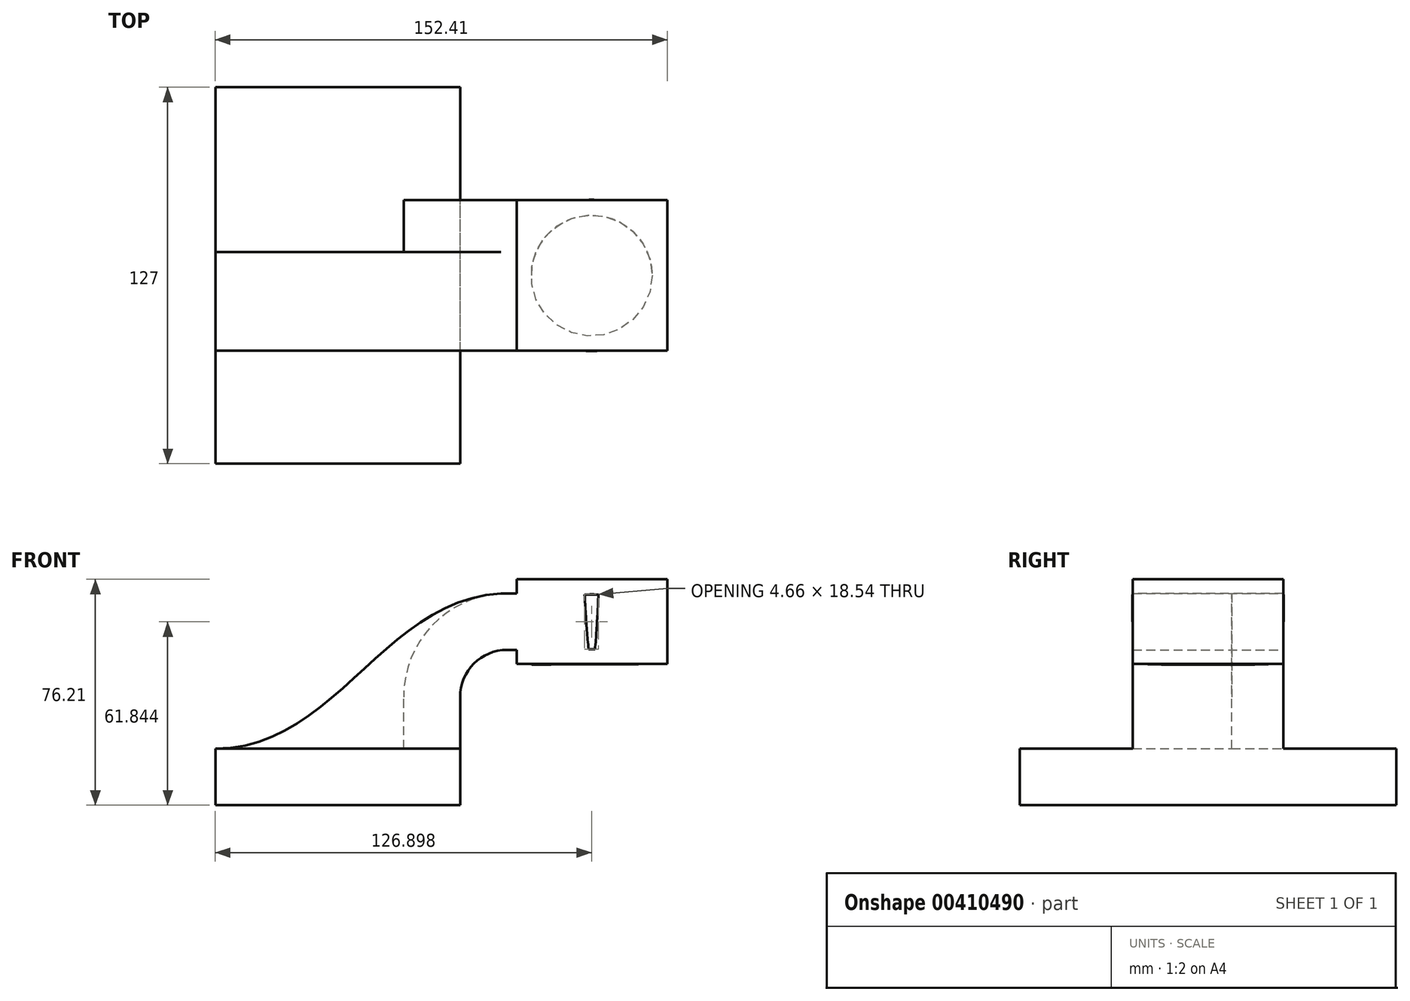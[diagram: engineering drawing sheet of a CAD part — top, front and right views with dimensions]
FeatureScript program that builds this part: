
annotation { "Feature Type Name" : "Feature", "Feature Type Description" : "" }
export const myFeature = defineFeature(function(context is Context, id is Id, definition is map)
    precondition{}
    {
        {
            var Q0;
            Q0=qCreatedBy(makeId("Front.planeOp"),FACE);
            var sketch = newSketch(context, id + "F0", { "sketchPlane" : qUnion([Q0])});
            skLineSegment(sketch, "E0.bottom", {"start": v(41.28, -9.52) * mm, "end": v(-41.28, -9.53) * mm});
            skLineSegment(sketch, "E0.top", {"start": v(41.27, 9.53) * mm, "end": v(-41.28, 9.53) * mm});
            skLineSegment(sketch, "E0.left", {"start": v(41.28, -9.52) * mm, "end": v(41.28, 9.53) * mm});
            skLineSegment(sketch, "E0.right", {"start": v(-41.28, -9.53) * mm, "end": v(-41.28, 9.53) * mm});
            skPoint(sketch, "E0.middle", {"position": v(0, 0) * mm});
            skLineSegment(sketch, "E1.bottom", {"start": v(111.12, 38.1) * mm, "end": v(60.33, 38.1) * mm});
            skLineSegment(sketch, "E1.top", {"start": v(111.12, 66.68) * mm, "end": v(60.33, 66.68) * mm});
            skLineSegment(sketch, "E1.left", {"start": v(111.12, 38.1) * mm, "end": v(111.12, 66.68) * mm});
            skLineSegment(sketch, "E1.right", {"start": v(60.33, 38.1) * mm, "end": v(60.33, 66.68) * mm});
            skPoint(sketch, "E1.middle", {"position": v(85.72, 52.39) * mm});
            skLineSegment(sketch, "E2", {"start": v(41.27, 9.53) * mm, "end": v(41.27, 27) * mm});
            skArc(sketch, "E3", {"start": v(41.27, 27) * mm, "mid": v(45.92, 38.23) * mm, "end": v(57.15, 42.88) * mm});
            skLineSegment(sketch, "E4", {"start": v(57.15, 42.88) * mm, "end": v(85.6, 42.88) * mm});
            skLineSegment(sketch, "E5.0", {"start": v(57.15, 61.93) * mm, "end": v(85.6, 61.93) * mm});
            skArc(sketch, "E5.1", {"start": v(22.23, 27) * mm, "mid": v(32.45, 51.7) * mm, "end": v(57.15, 61.93) * mm});
            skLineSegment(sketch, "E5.2", {"start": v(22.22, 9.53) * mm, "end": v(22.22, 27) * mm});
            skLineSegment(sketch, "E6", {"start": v(85.72, 38.1) * mm, "end": v(85.6, 66.68) * mm});
            skFitSpline(sketch, "E7", {"points": [v(-41.28, 9.53) * mm, v(57.15, 61.93) * mm], "startDerivative": vector(123.83, 0) * mm, "endDerivative": vector(124, 1.06) * mm});
            skSolve(sketch);
        }
        {
            var Q0;
            Q0=makeQuery(id+"F0.imprint","IMPRINT",FACE,{"disambiguationData":[TD([[makeQuery(id+"F0.imprint","IMPRINT",EDGE,{"derivedFrom":sQuery(id+"F0.wireOp",EDGE,"E0.bottom")}),-1.0]])]});
            extrude(context, id + "F1", {"entities" : qUnion([Q0]), "endBound" : BoundingType.SYMMETRIC, "depth" : 127 * mm});
        }
        {
            var Q0;
            {var subQ1=sQuery(id+"F0.wireOp",EDGE,"E2");Q0=makeQuery(id+"F0.imprint","IMPRINT",FACE,{"disambiguationData":[TD([[makeQuery(id+"F0.imprint","IMPRINT",EDGE,{"derivedFrom":subQ1}),1.0]])]});}
            extrude(context, id + "F2", {"entities" : qUnion([Q0]), "operationType" : NewBodyOperationType.ADD, "endBound" : BoundingType.SYMMETRIC, "depth" : 50.8 * mm});
        }
        {
            var Q0;
            {var subQ3=sQuery(id+"F0.wireOp",EDGE,"E5.2");Q0=makeQuery(id+"F0.imprint","IMPRINT",FACE,{"disambiguationData":[TD([[makeQuery(id+"F0.imprint","IMPRINT",EDGE,{"derivedFrom":subQ3}),1.0]])]});}
            extrude(context, id + "F3", {"entities" : qUnion([Q0]), "operationType" : NewBodyOperationType.ADD, "endBound" : BoundingType.SYMMETRIC, "depth" : 15.88 * mm});
        }
        {
            var Q0;
            {var subQ0=sQuery(id+"F0.wireOp",EDGE,"E1.left");Q0=makeQuery(id+"F0.imprint","IMPRINT",FACE,{"disambiguationData":[TD([[makeQuery(id+"F0.imprint","IMPRINT",EDGE,{"derivedFrom":subQ0}),1.0]])]});}
            var Q1;
            Q1=sQuery(id+"F0.wireOp",EDGE,"E6");
            revolve(context, id + "F4", {"operationType" : NewBodyOperationType.ADD, "entities" : qUnion([Q0]), "axis" : qUnion([Q1]), "revolveType" : RevolveType.FULL});
        }
        {
            var Q0;
            Q0=makeQuery(id+"F1.opExtrude","CAP_EDGE",EDGE,{"disambiguationData":[OSD([sQuery(id+"F0.wireOp",EDGE,"E0.right")])],"isStart":false});
            var Q1;
            Q1=makeQuery(id+"F1.opExtrude","CAP_EDGE",EDGE,{"disambiguationData":[OSD([sQuery(id+"F0.wireOp",EDGE,"E0.left")])],"isStart":false});
            var Q2;
            Q2=makeQuery(id+"F1.opExtrude","CAP_EDGE",EDGE,{"disambiguationData":[OSD([sQuery(id+"F0.wireOp",EDGE,"E0.left")])],"isStart":true});
            var Q3;
            Q3=makeQuery(id+"F1.opExtrude","CAP_EDGE",EDGE,{"disambiguationData":[OSD([sQuery(id+"F0.wireOp",EDGE,"E0.right")])],"isStart":true});
            fillet(context, id + "F5", {"entities" : qUnion([Q0, Q1, Q2, Q3]), "radius" : 6.35 * mm, "tangentPropagation" : true, "allowEdgeOverflow" : false});
        }
        {
            var Q0;
            Q0=makeQuery(id+"F2.opExtrude","CAP_EDGE",EDGE,{"disambiguationData":[OSD([sQuery(id+"F0.wireOp",EDGE,"E5.1")])],"isStart":true});
            var Q1;
            Q1=makeQuery(id+"F2.opExtrude","CAP_EDGE",EDGE,{"disambiguationData":[OSD([sQuery(id+"F0.wireOp",EDGE,"E3")])],"isStart":true});
            var Q2;
            Q2=makeQuery(id+"F2.opExtrude","CAP_EDGE",EDGE,{"disambiguationData":[OSD([sQuery(id+"F0.wireOp",EDGE,"E5.1")])],"isStart":false});
            var Q3;
            Q3=makeQuery(id+"F2.opExtrude","CAP_EDGE",EDGE,{"disambiguationData":[OSD([sQuery(id+"F0.wireOp",EDGE,"E3")])],"isStart":false});
            fillet(context, id + "F6", {"entities" : qUnion([Q0, Q1, Q2, Q3]), "radius" : 8.9 * mm, "tangentPropagation" : true, "allowEdgeOverflow" : false});
        }
        {
            var Q0;
            Q0=makeQuery(id+"F3.opExtrude","CAP_EDGE",EDGE,{"disambiguationData":[OSD([sQuery(id+"F0.wireOp",EDGE,"E7")])],"isStart":false});
            var Q1;
            Q1=makeQuery(id+"F3.opExtrude","CAP_EDGE",EDGE,{"disambiguationData":[OSD([sQuery(id+"F0.wireOp",EDGE,"E7")])],"isStart":true});
            fillet(context, id + "F7", {"entities" : qUnion([Q0, Q1]), "radius" : 5.08 * mm, "tangentPropagation" : true, "allowEdgeOverflow" : false});
        }
        {
            var Q0;
            Q0=makeQuery(id+"F4.opRevolve","SWEPT_EDGE",EDGE,{"disambiguationData":[OSD([sQuery(id+"F0.wireOp",EDGE,"E1.top"),sQuery(id+"F0.wireOp",EDGE,"E1.left")])]});
            var Q1;
            Q1=makeQuery(id+"F4.opRevolve","SWEPT_EDGE",EDGE,{"disambiguationData":[OSD([sQuery(id+"F0.wireOp",EDGE,"E1.bottom"),sQuery(id+"F0.wireOp",EDGE,"E1.left")])]});
            chamfer(context, id + "F8", {"entities" : qUnion([Q0, Q1]), "width" : 5.08 * mm, "tangentPropagation" : true});
        }
        {
            var Q0;
            Q0=makeQuery(id+"F0.imprint","IMPRINT",FACE,{"disambiguationData":[TD([[makeQuery(id+"F0.imprint","IMPRINT",EDGE,{"derivedFrom":sQuery(id+"F0.wireOp",EDGE,"E0.bottom")}),-1.0]])]});
            extrude(context, id + "F9", {"entities" : qUnion([Q0]), "endBound" : BoundingType.SYMMETRIC, "depth" : 127 * mm});
        }
        {
            var Q0;
            {var subQ1=sQuery(id+"F0.wireOp",EDGE,"E2");Q0=makeQuery(id+"F0.imprint","IMPRINT",FACE,{"disambiguationData":[TD([[makeQuery(id+"F0.imprint","IMPRINT",EDGE,{"derivedFrom":subQ1}),1.0]])]});}
            var Q1;
            {var subQ6=sQuery(id+"F0.wireOp",EDGE,"E6");Q1=makeQuery(id+"F0.imprint","IMPRINT",FACE,{"disambiguationData":[TD([[makeQuery(id+"F0.imprint","IMPRINT",EDGE,{"derivedFrom":subQ6}),1.0]])]});}
            var Q2;
            {var subQ0=sQuery(id+"F0.wireOp",EDGE,"E1.left");Q2=makeQuery(id+"F0.imprint","IMPRINT",FACE,{"disambiguationData":[TD([[makeQuery(id+"F0.imprint","IMPRINT",EDGE,{"derivedFrom":subQ0}),1.0]])]});}
            extrude(context, id + "F10", {"entities" : qUnion([Q0, Q1, Q2]), "operationType" : NewBodyOperationType.ADD, "endBound" : BoundingType.SYMMETRIC, "depth" : 50.8 * mm});
        }
        {
            var Q0;
            {var subQ3=sQuery(id+"F0.wireOp",EDGE,"E5.2");Q0=makeQuery(id+"F0.imprint","IMPRINT",FACE,{"disambiguationData":[TD([[makeQuery(id+"F0.imprint","IMPRINT",EDGE,{"derivedFrom":subQ3}),1.0]])]});}
            extrude(context, id + "F11", {"entities" : qUnion([Q0]), "operationType" : NewBodyOperationType.ADD, "endBound" : BoundingType.SYMMETRIC, "depth" : 15.88 * mm});
        }
        {
            var Q0;
            Q0 = qSketchRegion(id + "F0", true);
            extrude(context, id + "F12", {"entities" : qUnion([Q0]), "operationType" : NewBodyOperationType.ADD, "depth" : 25.4 * mm});
        }
    });
